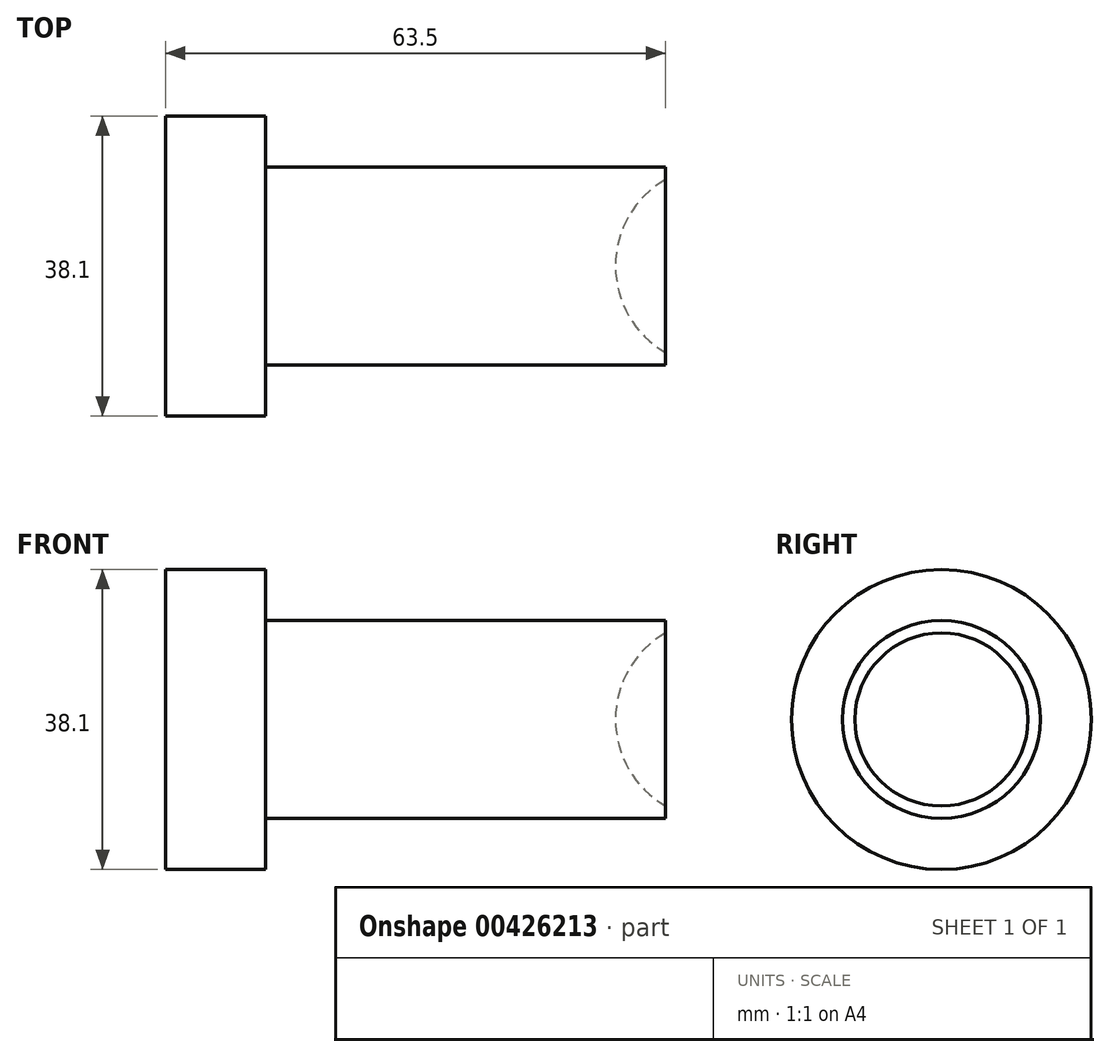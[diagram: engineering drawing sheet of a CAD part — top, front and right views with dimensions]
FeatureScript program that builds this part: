
annotation { "Feature Type Name" : "Feature", "Feature Type Description" : "" }
export const myFeature = defineFeature(function(context is Context, id is Id, definition is map)
    precondition{}
    {
        {
            var Q0;
            Q0=qCreatedBy(makeId("Right.planeOp"),FACE);
            var sketch = newSketch(context, id + "F0", { "sketchPlane" : qUnion([Q0])});
            skCircle(sketch, "E0", {"center": v(0, 0) * mm, "radius": 19.05 * mm});
            skSolve(sketch);
        }
        {
            var Q0;
            Q0 = qSketchRegion(id + "F0", true);
            extrude(context, id + "F1", {"entities" : qUnion([Q0]), "depth" : 12.7 * mm});
        }
        {
            var Q0;
            Q0=makeQuery(id+"F1.opExtrude","CAP_FACE",FACE,{"disambiguationData":[OSD([sQuery(id+"F0.wireOp",EDGE,"E0")])],"isStart":false});
            var sketch = newSketch(context, id + "F2", { "sketchPlane" : qUnion([Q0])});
            skCircle(sketch, "E1", {"center": v(0, 0) * mm, "radius": 12.57 * mm});
            skSolve(sketch);
        }
        {
            var Q0;
            Q0 = qSketchRegion(id + "F2", true);
            extrude(context, id + "F3", {"entities" : qUnion([Q0]), "operationType" : NewBodyOperationType.ADD, "depth" : 50.8 * mm});
        }
        {
            var Q0;
            Q0=qCreatedBy(makeId("Front.planeOp"),FACE);
            var sketch = newSketch(context, id + "F4", { "sketchPlane" : qUnion([Q0])});
            skArc(sketch, "E2", {"start": v(69.85, 12.7) * mm, "mid": v(57.15, 0) * mm, "end": v(69.85, -12.7) * mm});
            skLineSegment(sketch, "E3", {"start": v(69.85, 12.7) * mm, "end": v(69.85, -12.7) * mm});
            skLineSegment(sketch, "E4", {"start": v(69.85, 12.7) * mm, "end": v(69.85, 21.61) * mm, "construction": true});
            skSolve(sketch);
        }
        {
            var Q0;
            Q0=makeQuery(id+"F4.imprint","IMPRINT",FACE,{"disambiguationData":[TD([[makeQuery(id+"F4.imprint","IMPRINT",EDGE,{"derivedFrom":sQuery(id+"F4.wireOp",EDGE,"E2")}),1.0]])]});
            var Q1;
            Q1=sQuery(id+"F4.wireOp",EDGE,"E4");
            revolve(context, id + "F5", {"operationType" : NewBodyOperationType.REMOVE, "entities" : qUnion([Q0]), "axis" : qUnion([Q1]), "revolveType" : RevolveType.FULL, "oppositeDirection" : true});
        }
    });
